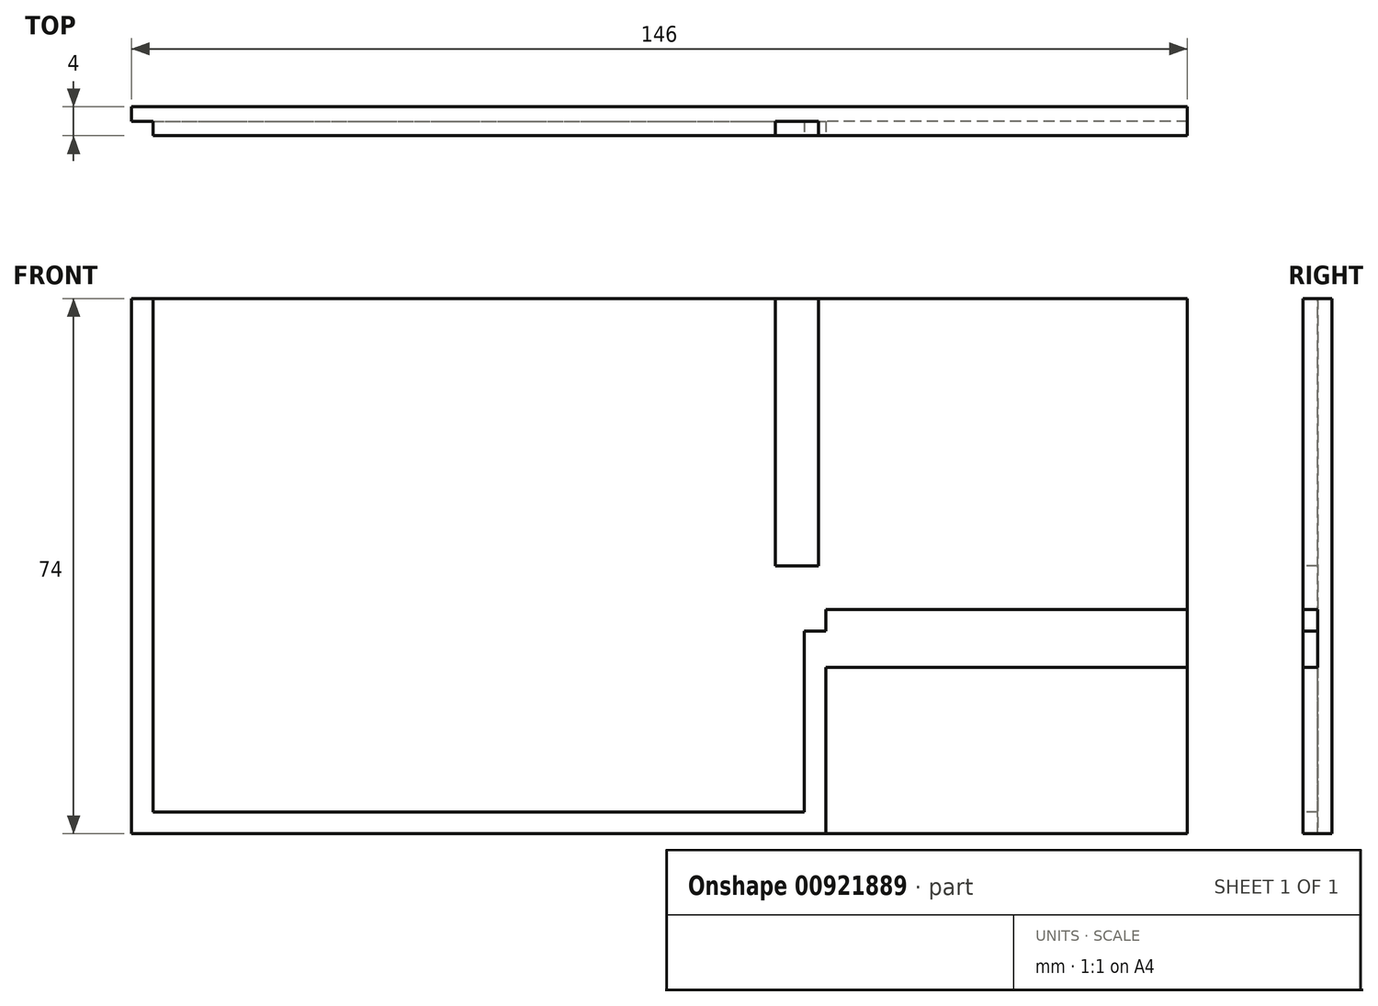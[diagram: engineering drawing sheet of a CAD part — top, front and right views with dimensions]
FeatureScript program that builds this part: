
annotation { "Feature Type Name" : "Feature", "Feature Type Description" : "" }
export const myFeature = defineFeature(function(context is Context, id is Id, definition is map)
    precondition{}
    {
        {
            var Q0;
            Q0=qCreatedBy(makeId("Front.planeOp"),FACE);
            var sketch = newSketch(context, id + "F0", { "sketchPlane" : qUnion([Q0])});
            skLineSegment(sketch, "E0.bottom", {"start": v(0, 0) * mm, "end": v(146, 0) * mm});
            skLineSegment(sketch, "E0.top", {"start": v(0, 74) * mm, "end": v(146, 74) * mm});
            skLineSegment(sketch, "E0.left", {"start": v(0, 0) * mm, "end": v(0, 74) * mm});
            skLineSegment(sketch, "E0.right", {"start": v(146, 0) * mm, "end": v(146, 74) * mm});
            skSolve(sketch);
        }
        {
            var Q0;
            Q0=makeQuery(id+"F0.imprint","IMPRINT",FACE,{"disambiguationData":[TD([[makeQuery(id+"F0.imprint","IMPRINT",EDGE,{"derivedFrom":sQuery(id+"F0.wireOp",EDGE,"E0.bottom")}),1.0]])]});
            extrude(context, id + "F1", {"entities" : qUnion([Q0]), "depth" : 4 * mm, "offsetDistance" : 25 * mm});
        }
        {
            var Q0;
            Q0=makeQuery(id+"F1.opExtrude","CAP_FACE",FACE,{"disambiguationData":[OSD([sQuery(id+"F0.wireOp",EDGE,"E0.bottom"),sQuery(id+"F0.wireOp",EDGE,"E0.top"),sQuery(id+"F0.wireOp",EDGE,"E0.left"),sQuery(id+"F0.wireOp",EDGE,"E0.right")])],"isStart":false});
            var sketch = newSketch(context, id + "F2", { "sketchPlane" : qUnion([Q0])});
            skLineSegment(sketch, "E1", {"start": v(3, 74) * mm, "end": v(3, 3) * mm});
            skLineSegment(sketch, "E2", {"start": v(3, 3) * mm, "end": v(93, 3) * mm});
            skLineSegment(sketch, "E3", {"start": v(93, 3) * mm, "end": v(93, 23) * mm});
            skLineSegment(sketch, "E4", {"start": v(93, 23) * mm, "end": v(96, 23) * mm});
            skLineSegment(sketch, "E5", {"start": v(96, 23) * mm, "end": v(96, 0) * mm});
            skLineSegment(sketch, "E6", {"start": v(89, 74) * mm, "end": v(89, 37) * mm});
            skLineSegment(sketch, "E7", {"start": v(89, 37) * mm, "end": v(95, 37) * mm});
            skLineSegment(sketch, "E8", {"start": v(95, 37) * mm, "end": v(95, 74) * mm});
            skLineSegment(sketch, "E9", {"start": v(146, 23) * mm, "end": v(93, 23) * mm});
            skLineSegment(sketch, "E10", {"start": v(93, 23) * mm, "end": v(93, 28) * mm});
            skLineSegment(sketch, "E11", {"start": v(93, 28) * mm, "end": v(96, 28) * mm});
            skLineSegment(sketch, "E12", {"start": v(96, 28) * mm, "end": v(96, 31) * mm});
            skLineSegment(sketch, "E13", {"start": v(96, 31) * mm, "end": v(146, 31) * mm});
            skSolve(sketch);
        }
        {
            var Q0;
            {var subQ3=sQuery(id+"F2.wireOp",EDGE,"E1");Q0=makeQuery(id+"F2.imprint","IMPRINT",FACE,{"disambiguationData":[TD([[makeQuery(id+"F2.imprint","IMPRINT",EDGE,{"derivedFrom":subQ3}),-1.0]])]});}
            extrude(context, id + "F3", {"entities" : qUnion([Q0]), "operationType" : NewBodyOperationType.REMOVE, "oppositeDirection" : true, "depth" : 2 * mm, "offsetDistance" : 25 * mm});
        }
        {
            var Q0;
            {var subQ0=sQuery(id+"F2.wireOp",EDGE,"E6");Q0=makeQuery(id+"F2.imprint","IMPRINT",FACE,{"disambiguationData":[TD([[makeQuery(id+"F2.imprint","IMPRINT",EDGE,{"derivedFrom":subQ0}),1.0]])]});}
            extrude(context, id + "F4", {"entities" : qUnion([Q0]), "operationType" : NewBodyOperationType.REMOVE, "oppositeDirection" : true, "depth" : 2 * mm, "offsetDistance" : 25 * mm});
        }
        {
            var Q0;
            Q0=makeQuery(id+"F2.imprint","IMPRINT",FACE,{"disambiguationData":[TD([[makeQuery(id+"F2.imprint","IMPRINT",EDGE,{"derivedFrom":sQuery(id+"F2.wireOp",EDGE,"E4")}),1.0]])]});
            extrude(context, id + "F5", {"entities" : qUnion([Q0]), "operationType" : NewBodyOperationType.REMOVE, "oppositeDirection" : true, "depth" : 2 * mm, "offsetDistance" : 25 * mm});
        }
    });
